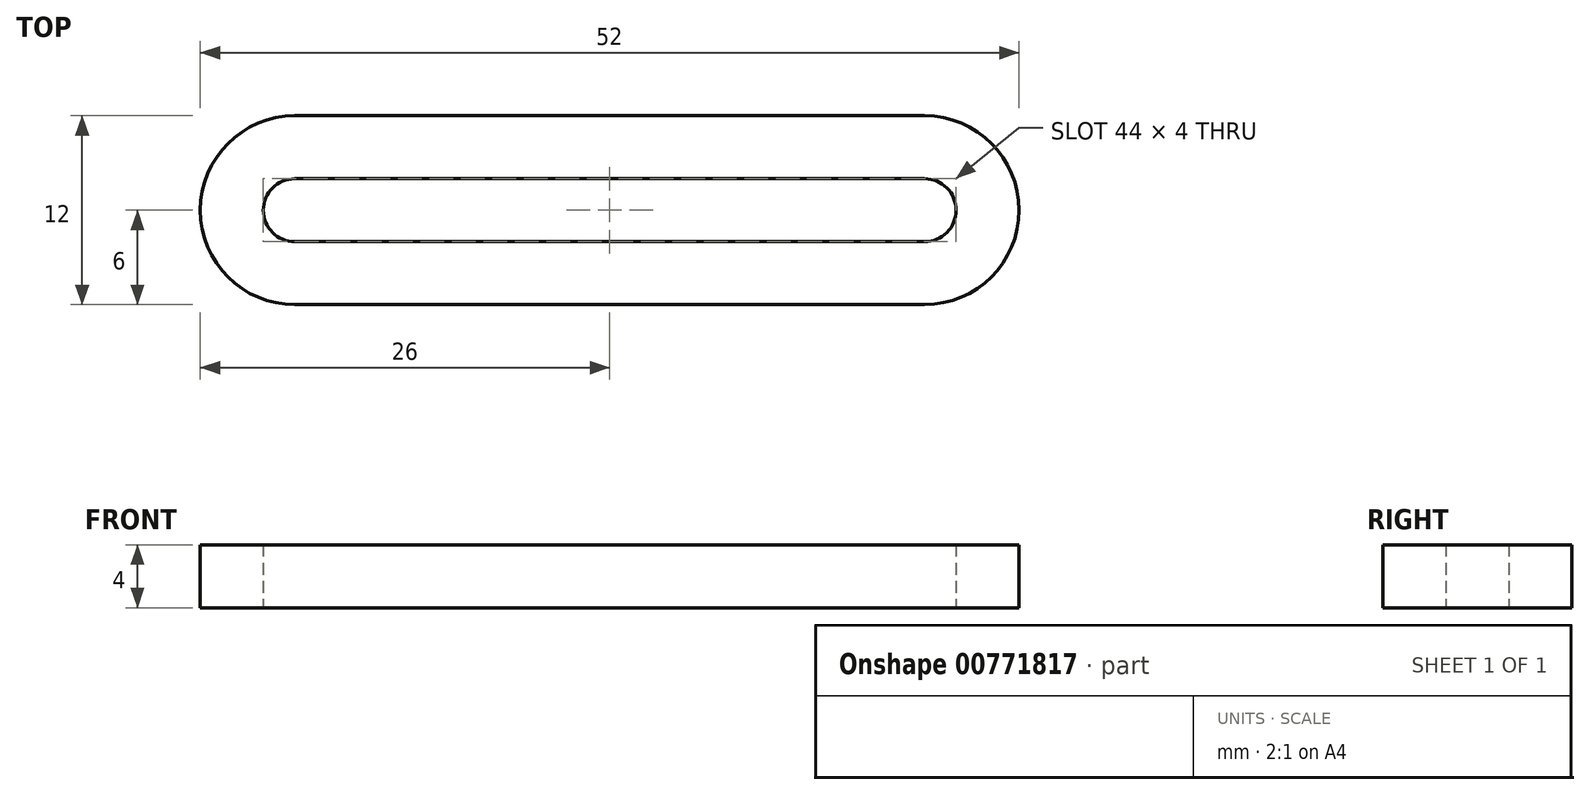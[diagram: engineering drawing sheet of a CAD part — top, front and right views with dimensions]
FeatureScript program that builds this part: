
annotation { "Feature Type Name" : "Feature", "Feature Type Description" : "" }
export const myFeature = defineFeature(function(context is Context, id is Id, definition is map)
    precondition{}
    {
        {
            var Q0;
            Q0=qCreatedBy(makeId("Top.planeOp"),FACE);
            var sketch = newSketch(context, id + "F0", { "sketchPlane" : qUnion([Q0])});
            skLineSegment(sketch, "E0.bottom", {"start": v(0, 8) * mm, "end": v(40, 8) * mm});
            skLineSegment(sketch, "E0.top", {"start": v(0, -4) * mm, "end": v(40, -4) * mm});
            skArc(sketch, "E1", {"start": v(0, 8) * mm, "mid": v(-6, 2) * mm, "end": v(0, -4) * mm});
            skArc(sketch, "E2", {"start": v(40, -4) * mm, "mid": v(46, 2) * mm, "end": v(40, 8) * mm});
            skSolve(sketch);
        }
        {
            var Q0;
            Q0=qCreatedBy(makeId("Top.planeOp"),FACE);
            var sketch = newSketch(context, id + "F1", { "sketchPlane" : qUnion([Q0])});
            skLineSegment(sketch, "E3.bottom", {"start": v(0, 0) * mm, "end": v(40, 0) * mm});
            skLineSegment(sketch, "E3.top", {"start": v(0, 4) * mm, "end": v(40, 4) * mm});
            skArc(sketch, "E4", {"start": v(0, 4) * mm, "mid": v(-2, 2) * mm, "end": v(0, 0) * mm});
            skArc(sketch, "E5", {"start": v(40, 0) * mm, "mid": v(42, 2) * mm, "end": v(40, 4) * mm});
            skSolve(sketch);
        }
        {
            var Q0;
            Q0 = qSketchRegion(id + "F0", true);
            extrude(context, id + "F2", {"entities" : qUnion([Q0]), "depth" : 4 * mm, "offsetDistance" : 25 * mm});
        }
        {
            var Q0;
            Q0 = qSketchRegion(id + "F1", true);
            extrude(context, id + "F3", {"entities" : qUnion([Q0]), "operationType" : NewBodyOperationType.REMOVE, "depth" : 25 * mm, "offsetDistance" : 25 * mm});
        }
    });
